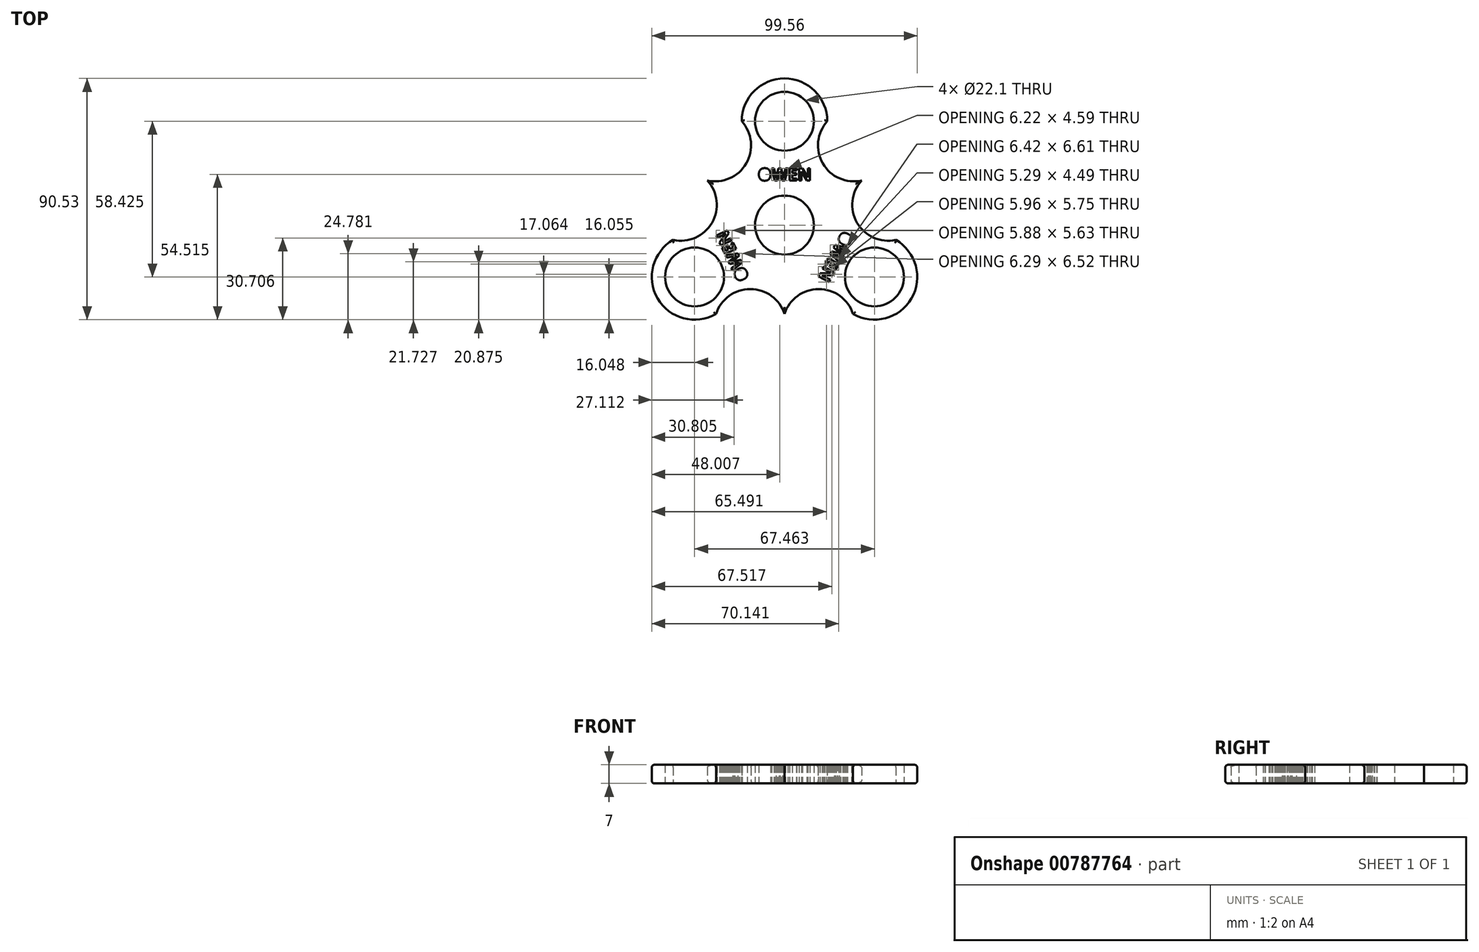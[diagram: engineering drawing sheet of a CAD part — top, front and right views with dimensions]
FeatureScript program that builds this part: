
annotation { "Feature Type Name" : "Feature", "Feature Type Description" : "" }
export const myFeature = defineFeature(function(context is Context, id is Id, definition is map)
    precondition{}
    {
        {
            var Q0;
            Q0=qCreatedBy(makeId("Top.planeOp"),FACE);
            var sketch = newSketch(context, id + "F0", { "sketchPlane" : qUnion([Q0])});
            skCircle(sketch, "E0", {"center": v(0, 0) * mm, "radius": 11.05 * mm});
            skCircle(sketch, "E1", {"center": v(0, 38.95) * mm, "radius": 11.05 * mm});
            skCircle(sketch, "E2.1.0", {"center": v(-33.73, -19.47) * mm, "radius": 11.05 * mm});
            skCircle(sketch, "E2.2.0", {"center": v(33.73, -19.48) * mm, "radius": 11.05 * mm});
            skArc(sketch, "E3", {"start": v(16.05, 38.95) * mm, "mid": v(0, 55) * mm, "end": v(-16.05, 38.95) * mm});
            skArc(sketch, "E4.1.0", {"start": v(-41.76, -5.58) * mm, "mid": v(-47.63, -27.5) * mm, "end": v(-25.7, -33.37) * mm});
            skArc(sketch, "E4.2.0", {"start": v(25.7, -33.37) * mm, "mid": v(47.63, -27.5) * mm, "end": v(41.76, -5.58) * mm});
            skArc(sketch, "E5", {"start": v(-41.76, -5.58) * mm, "mid": v(-27.21, 0.87) * mm, "end": v(-28.9, 16.69) * mm});
            skArc(sketch, "E6", {"start": v(-28.9, 16.69) * mm, "mid": v(-14.36, 23.13) * mm, "end": v(-16.05, 38.95) * mm});
            skArc(sketch, "E7.1.0", {"start": v(25.7, -33.37) * mm, "mid": v(12.85, -24) * mm, "end": v(0, -33.37) * mm});
            skArc(sketch, "E7.1.1", {"start": v(0, -33.37) * mm, "mid": v(-12.85, -24) * mm, "end": v(-25.7, -33.37) * mm});
            skArc(sketch, "E7.2.0", {"start": v(16.05, 38.95) * mm, "mid": v(14.36, 23.13) * mm, "end": v(28.9, 16.69) * mm});
            skArc(sketch, "E7.2.1", {"start": v(28.9, 16.69) * mm, "mid": v(27.21, 0.87) * mm, "end": v(41.76, -5.58) * mm});
            skText(sketch, "E8", { "text": "OWEN", "fontName": "OpenSans-Bold.ttf"});
            skText(sketch, "E9", { "text": "OWEN", "fontName": "OpenSans-Bold.ttf"});
            skText(sketch, "E10", { "text": "OWEN", "fontName": "OpenSans-Bold.ttf"});
            const initialGuessF0  = {"E8": [-0.01, 0.01669, 1, 0, 0.00463], "E9": [-0.01317, -0.01976, -0.42262, 0.9063, 0.00463], "E10": [0.02192, -0.00189, -0.46924, -0.88307, 0.00463]};
            skSetInitialGuess(sketch, initialGuessF0);
            skSolve(sketch);
        }
        {
            var Q0;
            Q0=makeQuery(id+"F0.imprint","IMPRINT",FACE,{"disambiguationData":[TD([[makeQuery(id+"F0.imprint","IMPRINT",EDGE,{"derivedFrom":sQuery(id+"F0.wireOp",EDGE,"E0")}),-1.0]])]});
            extrude(context, id + "F1", {"entities" : qUnion([Q0]), "depth" : 7 * mm, "offsetDistance" : 25 * mm});
        }
        {
            var Q0;
            Q0=makeQuery(id+"F1.opExtrude","CAP_EDGE",EDGE,{"disambiguationData":[OSD([sQuery(id+"F0.wireOp",EDGE,"E6")])],"isStart":false});
            var Q1;
            Q1=makeQuery(id+"F1.opExtrude","CAP_EDGE",EDGE,{"disambiguationData":[OSD([sQuery(id+"F0.wireOp",EDGE,"E3")])],"isStart":false});
            var Q2;
            Q2=makeQuery(id+"F1.opExtrude","CAP_EDGE",EDGE,{"disambiguationData":[OSD([sQuery(id+"F0.wireOp",EDGE,"E7.2.0")])],"isStart":false});
            var Q3;
            Q3=makeQuery(id+"F1.opExtrude","CAP_EDGE",EDGE,{"disambiguationData":[OSD([sQuery(id+"F0.wireOp",EDGE,"E7.2.1")])],"isStart":false});
            var Q4;
            Q4=makeQuery(id+"F1.opExtrude","CAP_EDGE",EDGE,{"disambiguationData":[OSD([sQuery(id+"F0.wireOp",EDGE,"E4.2.0")])],"isStart":false});
            var Q5;
            Q5=makeQuery(id+"F1.opExtrude","CAP_EDGE",EDGE,{"disambiguationData":[OSD([sQuery(id+"F0.wireOp",EDGE,"E7.1.0")])],"isStart":false});
            var Q6;
            Q6=makeQuery(id+"F1.opExtrude","CAP_EDGE",EDGE,{"disambiguationData":[OSD([sQuery(id+"F0.wireOp",EDGE,"E7.1.1")])],"isStart":false});
            var Q7;
            Q7=makeQuery(id+"F1.opExtrude","CAP_EDGE",EDGE,{"disambiguationData":[OSD([sQuery(id+"F0.wireOp",EDGE,"E5")])],"isStart":false});
            var Q8;
            Q8=makeQuery(id+"F1.opExtrude","CAP_EDGE",EDGE,{"disambiguationData":[OSD([sQuery(id+"F0.wireOp",EDGE,"E4.1.0")])],"isStart":false});
            var Q9;
            Q9=makeQuery(id+"F1.opExtrude","CAP_EDGE",EDGE,{"disambiguationData":[OSD([sQuery(id+"F0.wireOp",EDGE,"E7.1.1")])],"isStart":true});
            var Q10;
            Q10=makeQuery(id+"F1.opExtrude","CAP_EDGE",EDGE,{"disambiguationData":[OSD([sQuery(id+"F0.wireOp",EDGE,"E4.1.0")])],"isStart":true});
            var Q11;
            Q11=makeQuery(id+"F1.opExtrude","CAP_EDGE",EDGE,{"disambiguationData":[OSD([sQuery(id+"F0.wireOp",EDGE,"E5")])],"isStart":true});
            var Q12;
            Q12=makeQuery(id+"F1.opExtrude","CAP_EDGE",EDGE,{"disambiguationData":[OSD([sQuery(id+"F0.wireOp",EDGE,"E6")])],"isStart":true});
            var Q13;
            Q13=makeQuery(id+"F1.opExtrude","CAP_EDGE",EDGE,{"disambiguationData":[OSD([sQuery(id+"F0.wireOp",EDGE,"E3")])],"isStart":true});
            var Q14;
            Q14=makeQuery(id+"F1.opExtrude","CAP_EDGE",EDGE,{"disambiguationData":[OSD([sQuery(id+"F0.wireOp",EDGE,"E7.2.0")])],"isStart":true});
            var Q15;
            Q15=makeQuery(id+"F1.opExtrude","CAP_EDGE",EDGE,{"disambiguationData":[OSD([sQuery(id+"F0.wireOp",EDGE,"E7.2.1")])],"isStart":true});
            var Q16;
            Q16=makeQuery(id+"F1.opExtrude","CAP_EDGE",EDGE,{"disambiguationData":[OSD([sQuery(id+"F0.wireOp",EDGE,"E4.2.0")])],"isStart":true});
            var Q17;
            Q17=makeQuery(id+"F1.opExtrude","CAP_EDGE",EDGE,{"disambiguationData":[OSD([sQuery(id+"F0.wireOp",EDGE,"E7.1.0")])],"isStart":true});
            fillet(context, id + "F2", {"entities" : qUnion([Q0, Q1, Q2, Q3, Q4, Q5, Q6, Q7, Q8, Q9, Q10, Q11, Q12, Q13, Q14, Q15, Q16, Q17]), "radius" : 1 * mm, "tangentPropagation" : true, "allowEdgeOverflow" : false});
        }
    });
